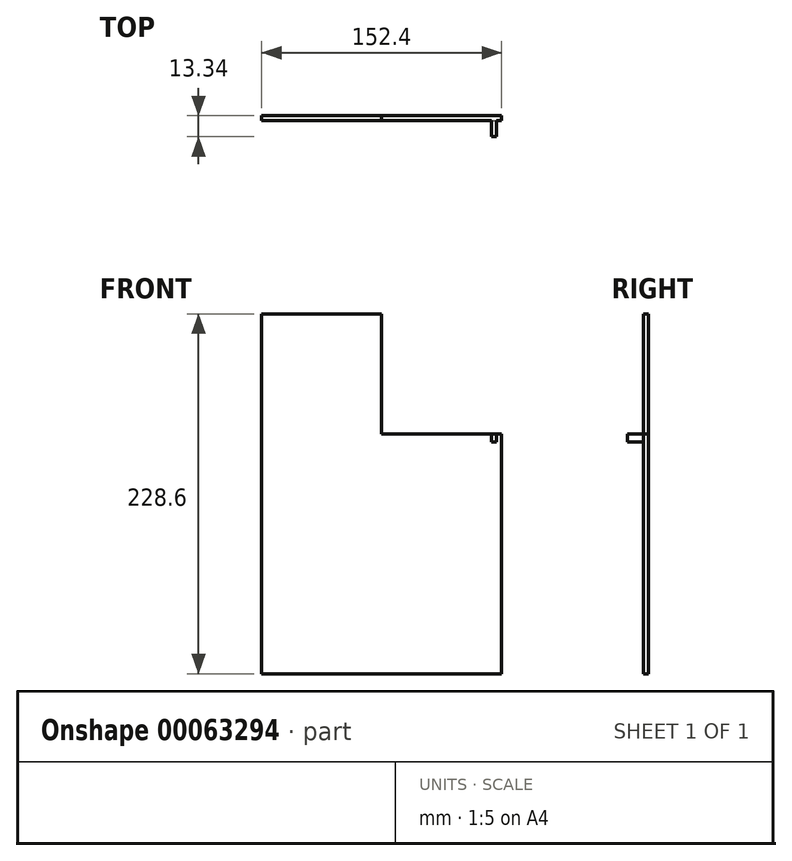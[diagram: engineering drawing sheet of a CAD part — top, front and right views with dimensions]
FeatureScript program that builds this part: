
annotation { "Feature Type Name" : "Feature", "Feature Type Description" : "" }
export const myFeature = defineFeature(function(context is Context, id is Id, definition is map)
    precondition{}
    {
        {
            var Q0;
            Q0=qCreatedBy(makeId("Front.planeOp"),FACE);
            var sketch = newSketch(context, id + "F0", { "sketchPlane" : qUnion([Q0])});
            skLineSegment(sketch, "E0.rect.bottom", {"start": v(76.2, 114.3) * mm, "end": v(-76.2, 114.3) * mm});
            skLineSegment(sketch, "E0.rect.top", {"start": v(76.2, -114.3) * mm, "end": v(-76.2, -114.3) * mm});
            skLineSegment(sketch, "E0.rect.left", {"start": v(76.2, 114.3) * mm, "end": v(76.2, -114.3) * mm});
            skLineSegment(sketch, "E0.rect.right", {"start": v(-76.2, 114.3) * mm, "end": v(-76.2, -114.3) * mm});
            skPoint(sketch, "E0.rect.middle", {"position": v(0, 0) * mm});
            skSolve(sketch);
        }
        {
            var Q0;
            Q0=makeQuery(id+"F0.imprint","IMPRINT",FACE,{"disambiguationData":[TD([[makeQuery(id+"F0.imprint","IMPRINT",EDGE,{"derivedFrom":sQuery(id+"F0.wireOp",EDGE,"E0.rect.bottom")}),1.0]])]});
            extrude(context, id + "F1", {"entities" : qUnion([Q0]), "depth" : 3.17 * mm, "symmetric" : true});
        }
        {
            var Q0;
            Q0=makeQuery(id+"F1.opExtrude","CAP_FACE",FACE,{"disambiguationData":[OSD([sQuery(id+"F0.wireOp",EDGE,"E0.rect.bottom"),sQuery(id+"F0.wireOp",EDGE,"E0.rect.top"),sQuery(id+"F0.wireOp",EDGE,"E0.rect.left"),sQuery(id+"F0.wireOp",EDGE,"E0.rect.right")])],"isStart":false});
            var sketch = newSketch(context, id + "F2", { "sketchPlane" : qUnion([Q0])});
            skLineSegment(sketch, "E1.bottom", {"start": v(76.2, 114.3) * mm, "end": v(0, 114.3) * mm});
            skLineSegment(sketch, "E1.top", {"start": v(76.2, 38.1) * mm, "end": v(0, 38.1) * mm});
            skLineSegment(sketch, "E1.left", {"start": v(76.2, 114.3) * mm, "end": v(76.2, 38.1) * mm});
            skLineSegment(sketch, "E1.right", {"start": v(0, 114.3) * mm, "end": v(0, 38.1) * mm});
            skSolve(sketch);
        }
        {
            var Q0;
            Q0=qSketchRegion(id+"F2",true);
            extrude(context, id + "F3", {"entities" : qUnion([Q0]), "operationType" : NewBodyOperationType.REMOVE, "endBound" : BoundingType.THROUGH_ALL, "oppositeDirection" : true, "depth" : 25.4 * mm});
        }
        {
            var Q0;
            Q0=makeQuery(id+"F1.opExtrude","CAP_FACE",FACE,{"disambiguationData":[OSD([sQuery(id+"F0.wireOp",EDGE,"E0.rect.bottom"),sQuery(id+"F0.wireOp",EDGE,"E0.rect.top"),sQuery(id+"F0.wireOp",EDGE,"E0.rect.left"),sQuery(id+"F0.wireOp",EDGE,"E0.rect.right")])],"isStart":false});
            var sketch = newSketch(context, id + "F4", { "sketchPlane" : qUnion([Q0])});
            skLineSegment(sketch, "E2.bottom", {"start": v(69.85, 38.1) * mm, "end": v(73.03, 38.1) * mm});
            skLineSegment(sketch, "E2.top", {"start": v(69.85, 32.95) * mm, "end": v(73.03, 32.95) * mm});
            skLineSegment(sketch, "E2.left", {"start": v(69.85, 38.1) * mm, "end": v(69.85, 32.95) * mm});
            skLineSegment(sketch, "E2.right", {"start": v(73.03, 38.1) * mm, "end": v(73.03, 32.95) * mm});
            skSolve(sketch);
        }
        {
            var Q0;
            Q0 = qSketchRegion(id + "F4", true);
            extrude(context, id + "F5", {"entities" : qUnion([Q0]), "operationType" : NewBodyOperationType.ADD, "depth" : 10.16 * mm});
        }
    });
